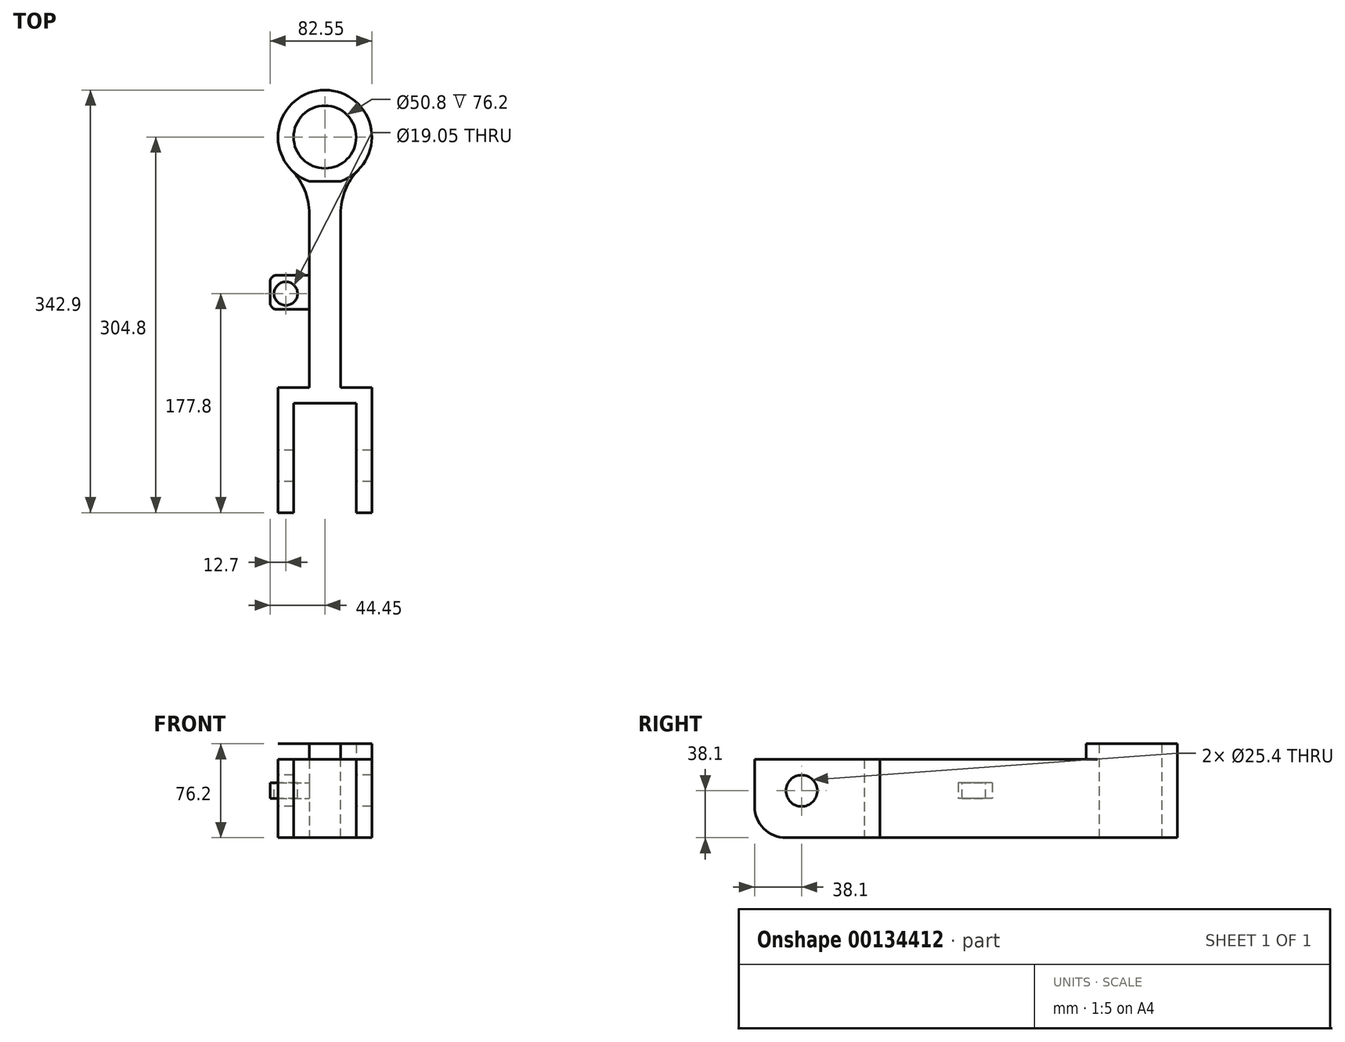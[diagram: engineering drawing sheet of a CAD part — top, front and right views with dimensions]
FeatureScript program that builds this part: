
annotation { "Feature Type Name" : "Feature", "Feature Type Description" : "" }
export const myFeature = defineFeature(function(context is Context, id is Id, definition is map)
    precondition{}
    {
        {
            var Q0;
            Q0=qCreatedBy(makeId("Top.planeOp"),FACE);
            var sketch = newSketch(context, id + "F0", { "sketchPlane" : qUnion([Q0])});
            skCircle(sketch, "E0", {"center": v(0, 203.2) * mm, "radius": 25.4 * mm});
            skCircle(sketch, "E1", {"center": v(0, 203.2) * mm, "radius": 38.1 * mm});
            skLineSegment(sketch, "E2", {"start": v(12.7, 0) * mm, "end": v(38.1, 0) * mm});
            skLineSegment(sketch, "E3", {"start": v(-12.7, 0) * mm, "end": v(-38.1, 0) * mm});
            skLineSegment(sketch, "E4", {"start": v(-38.1, 0) * mm, "end": v(-38.1, -101.6) * mm});
            skLineSegment(sketch, "E5", {"start": v(38.1, 0) * mm, "end": v(38.1, -101.6) * mm});
            skLineSegment(sketch, "E6", {"start": v(-12.7, 0) * mm, "end": v(-12.7, 167.28) * mm});
            skLineSegment(sketch, "E7", {"start": v(12.7, 0) * mm, "end": v(12.7, 167.28) * mm});
            skLineSegment(sketch, "E8", {"start": v(25.4, -12.7) * mm, "end": v(25.4, -101.6) * mm});
            skLineSegment(sketch, "E9", {"start": v(-25.4, -12.7) * mm, "end": v(-25.4, -101.6) * mm});
            skLineSegment(sketch, "E10", {"start": v(-38.1, -101.6) * mm, "end": v(-25.4, -101.6) * mm});
            skLineSegment(sketch, "E11", {"start": v(25.4, -101.6) * mm, "end": v(38.1, -101.6) * mm});
            skLineSegment(sketch, "E12", {"start": v(-25.4, -12.7) * mm, "end": v(25.4, -12.7) * mm});
            skPoint(sketch, "E13", {"position": v(0, 0) * mm});
            skSolve(sketch);
        }
        {
            var Q0;
            Q0 = qSketchRegion(id + "F0", true);
            extrude(context, id + "F1", {"entities" : qUnion([Q0]), "depth" : 76.2 * mm});
        }
        {
            var Q0;
            Q0=makeQuery(id+"F1.opExtrude","CAP_FACE",FACE,{"disambiguationData":[OSD([sQuery(id+"F0.wireOp",EDGE,"E0"),sQuery(id+"F0.wireOp",EDGE,"E1"),sQuery(id+"F0.wireOp",EDGE,"E2"),sQuery(id+"F0.wireOp",EDGE,"E3"),sQuery(id+"F0.wireOp",EDGE,"E4"),sQuery(id+"F0.wireOp",EDGE,"E5"),sQuery(id+"F0.wireOp",EDGE,"E6"),sQuery(id+"F0.wireOp",EDGE,"E7"),sQuery(id+"F0.wireOp",EDGE,"E8"),sQuery(id+"F0.wireOp",EDGE,"E9"),sQuery(id+"F0.wireOp",EDGE,"E10"),sQuery(id+"F0.wireOp",EDGE,"E11"),sQuery(id+"F0.wireOp",EDGE,"E12")])],"isStart":false});
            var sketch = newSketch(context, id + "F2", { "sketchPlane" : qUnion([Q0])});
            skLineSegment(sketch, "E14", {"start": v(-12.7, 167.28) * mm, "end": v(12.7, 167.28) * mm});
            skLineSegment(sketch, "E15", {"start": v(12.7, 167.28) * mm, "end": v(12.7, 0) * mm});
            skLineSegment(sketch, "E16", {"start": v(12.7, 0) * mm, "end": v(-12.7, 0) * mm});
            skLineSegment(sketch, "E17", {"start": v(-12.7, 0) * mm, "end": v(-12.7, 167.28) * mm});
            skSolve(sketch);
        }
        {
            var Q0;
            Q0 = qSketchRegion(id + "F2", true);
            extrude(context, id + "F3", {"entities" : qUnion([Q0]), "operationType" : NewBodyOperationType.REMOVE, "oppositeDirection" : true, "depth" : 12.7 * mm});
        }
        {
            var Q0;
            {var subQ0=sQuery(id+"F0.wireOp",EDGE,"E5");var subQ1=sQuery(id+"F0.wireOp",EDGE,"E12");var subQ2=sQuery(id+"F0.wireOp",EDGE,"E4");var subQ3=sQuery(id+"F0.wireOp",EDGE,"E3");var subQ4=sQuery(id+"F0.wireOp",EDGE,"E10");var subQ5=sQuery(id+"F0.wireOp",EDGE,"E2");var subQ6=sQuery(id+"F0.wireOp",EDGE,"E8");var subQ7=sQuery(id+"F0.wireOp",EDGE,"E9");var subQ8=sQuery(id+"F0.wireOp",EDGE,"E11");Q0=makeQuery(id+"F3.boolean.opBoolean","SPLIT",FACE,{"disambiguationData":[TD([makeQuery(id+"F1.opExtrude","SWEPT_FACE",FACE,{"disambiguationData":[OSD([subQ5])]})])],"derivedFrom":makeQuery(id+"F1.opExtrude","CAP_FACE",FACE,{"disambiguationData":[OSD([sQuery(id+"F0.wireOp",EDGE,"E0"),sQuery(id+"F0.wireOp",EDGE,"E1"),subQ5,subQ3,subQ2,subQ0,sQuery(id+"F0.wireOp",EDGE,"E6"),sQuery(id+"F0.wireOp",EDGE,"E7"),subQ6,subQ7,subQ4,subQ8,subQ1])],"isStart":false})});}
            extrude(context, id + "F4", {"entities" : qUnion([Q0]), "operationType" : NewBodyOperationType.REMOVE, "oppositeDirection" : true, "depth" : 12.7 * mm});
        }
        {
            var Q0;
            Q0=makeQuery(id+"F1.opExtrude","SWEPT_FACE",FACE,{"disambiguationData":[OSD([sQuery(id+"F0.wireOp",EDGE,"E4")])]});
            var sketch = newSketch(context, id + "F5", { "sketchPlane" : qUnion([Q0])});
            skCircle(sketch, "E18", {"center": v(63.5, 38.1) * mm, "radius": 12.7 * mm});
            skSolve(sketch);
        }
        {
            var Q0;
            Q0 = qSketchRegion(id + "F5", true);
            extrude(context, id + "F6", {"entities" : qUnion([Q0]), "operationType" : NewBodyOperationType.REMOVE, "oppositeDirection" : true, "depth" : 254 * mm});
        }
        {
            var Q0;
            Q0=makeQuery(id+"F3.boolean.opBoolean","SPLIT",EDGE,{"derivedFrom":makeQuery(id+"F1.opExtrude","SWEPT_EDGE",EDGE,{"disambiguationData":[OSD([sQuery(id+"F0.wireOp",EDGE,"E1"),sQuery(id+"F0.wireOp",EDGE,"E6")])]})});
            var Q1;
            Q1=makeQuery(id+"F3.boolean.opBoolean","SPLIT",EDGE,{"derivedFrom":makeQuery(id+"F1.opExtrude","SWEPT_EDGE",EDGE,{"disambiguationData":[OSD([sQuery(id+"F0.wireOp",EDGE,"E1"),sQuery(id+"F0.wireOp",EDGE,"E7")])]})});
            fillet(context, id + "F7", {"entities" : qUnion([Q0, Q1]), "radius" : 50.8 * mm, "tangentPropagation" : true, "allowEdgeOverflow" : false});
        }
        {
            var Q0;
            Q0=makeQuery(id+"F4.boolean.opBoolean","COPY",EDGE,{"derivedFrom":makeQuery(id+"F4.opExtrude","CAP_EDGE",EDGE,{"disambiguationData":[OSD([sQuery(id+"F0.wireOp",EDGE,"E10")])],"isStart":false})});
            var Q1;
            Q1=makeQuery(id+"F1.opExtrude","CAP_EDGE",EDGE,{"disambiguationData":[OSD([sQuery(id+"F0.wireOp",EDGE,"E10")])],"isStart":true});
            var Q2;
            Q2=makeQuery(id+"F4.boolean.opBoolean","COPY",EDGE,{"derivedFrom":makeQuery(id+"F4.opExtrude","CAP_EDGE",EDGE,{"disambiguationData":[OSD([sQuery(id+"F0.wireOp",EDGE,"E11")])],"isStart":false})});
            var Q3;
            Q3=makeQuery(id+"F1.opExtrude","CAP_EDGE",EDGE,{"disambiguationData":[OSD([sQuery(id+"F0.wireOp",EDGE,"E11")])],"isStart":true});
            fillet(context, id + "F8", {"entities" : qUnion([Q0, Q1, Q2, Q3]), "radius" : 25.4 * mm, "tangentPropagation" : true, "allowEdgeOverflow" : false});
        }
        {
            var Q0;
            Q0=makeQuery(id+"F1.opExtrude","SWEPT_FACE",FACE,{"disambiguationData":[OSD([sQuery(id+"F0.wireOp",EDGE,"E6")])]});
            var sketch = newSketch(context, id + "F9", { "sketchPlane" : qUnion([Q0])});
            skLineSegment(sketch, "E19.bottom", {"start": v(-91.08, 44.45) * mm, "end": v(-63.5, 44.45) * mm});
            skLineSegment(sketch, "E19.top", {"start": v(-91.08, 31.75) * mm, "end": v(-63.5, 31.75) * mm});
            skLineSegment(sketch, "E19.left", {"start": v(-91.08, 44.45) * mm, "end": v(-91.08, 31.75) * mm});
            skLineSegment(sketch, "E19.right", {"start": v(-63.5, 44.45) * mm, "end": v(-63.5, 31.75) * mm});
            skSolve(sketch);
        }
        {
            var Q0;
            Q0 = qSketchRegion(id + "F9", true);
            extrude(context, id + "F10", {"entities" : qUnion([Q0]), "operationType" : NewBodyOperationType.ADD, "depth" : 31.75 * mm});
        }
        {
            var Q0;
            Q0=makeQuery(id+"F10.opExtrude","SWEPT_FACE",FACE,{"disambiguationData":[OSD([sQuery(id+"F9.wireOp",EDGE,"E19.bottom")])]});
            var sketch = newSketch(context, id + "F11", { "sketchPlane" : qUnion([Q0])});
            skCircle(sketch, "E20", {"center": v(-31.75, 76.2) * mm, "radius": 9.53 * mm});
            skSolve(sketch);
        }
        {
            var Q0;
            Q0 = qSketchRegion(id + "F11", true);
            extrude(context, id + "F12", {"entities" : qUnion([Q0]), "operationType" : NewBodyOperationType.REMOVE, "oppositeDirection" : true, "depth" : 25.4 * mm});
        }
        {
            var Q0;
            Q0=makeQuery(id+"F10.opExtrude","CAP_EDGE",EDGE,{"disambiguationData":[OSD([sQuery(id+"F9.wireOp",EDGE,"E19.right")])],"isStart":false});
            var Q1;
            Q1=makeQuery(id+"F10.opExtrude","CAP_EDGE",EDGE,{"disambiguationData":[OSD([sQuery(id+"F9.wireOp",EDGE,"E19.left")])],"isStart":false});
            fillet(context, id + "F13", {"entities" : qUnion([Q0, Q1]), "radius" : 5.08 * mm, "tangentPropagation" : true, "allowEdgeOverflow" : false});
        }
    });
